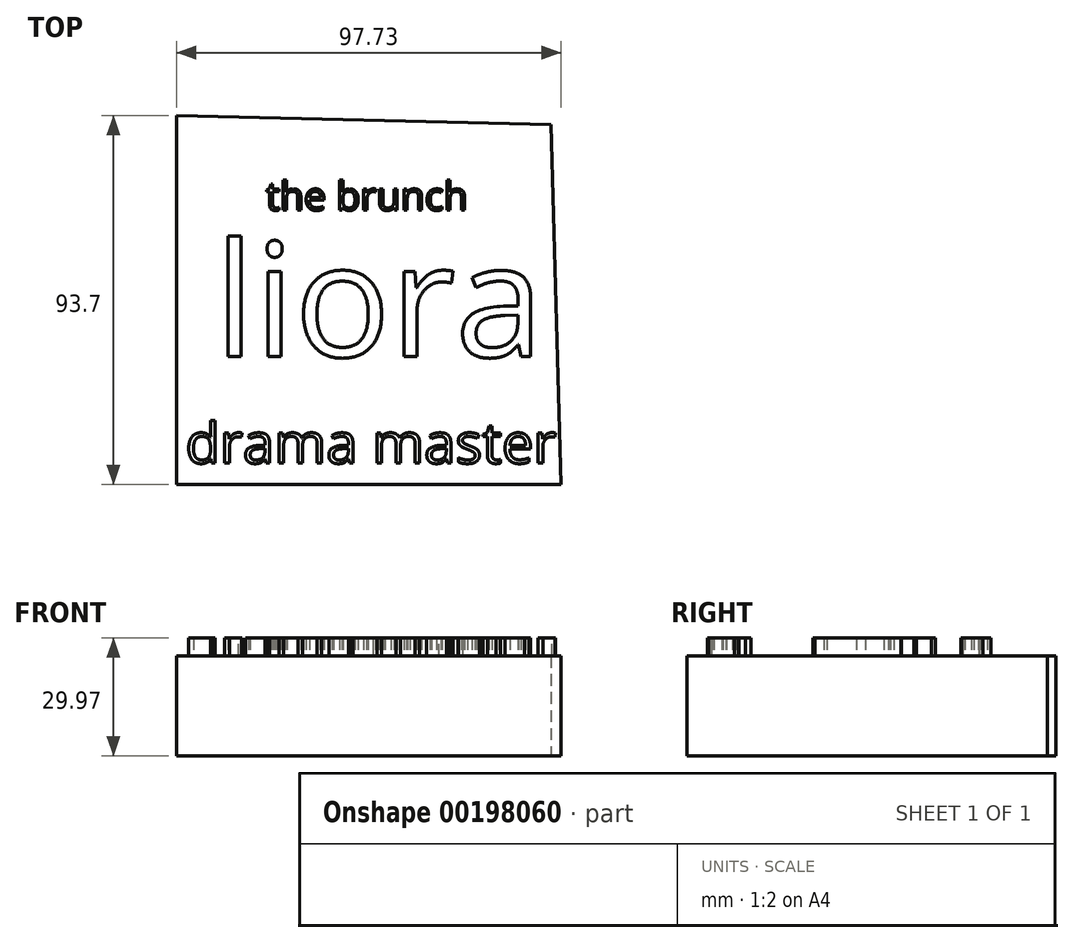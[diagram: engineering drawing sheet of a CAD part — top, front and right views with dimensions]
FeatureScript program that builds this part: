
annotation { "Feature Type Name" : "Feature", "Feature Type Description" : "" }
export const myFeature = defineFeature(function(context is Context, id is Id, definition is map)
    precondition{}
    {
        {
            var Q0;
            Q0=qCreatedBy(makeId("Top.planeOp"),FACE);
            var sketch = newSketch(context, id + "F0", { "sketchPlane" : qUnion([Q0])});
            skLineSegment(sketch, "E0", {"start": v(-49.97, 46) * mm, "end": v(-49.97, -47.7) * mm});
            skLineSegment(sketch, "E1", {"start": v(-49.97, -47.7) * mm, "end": v(47.76, -47.7) * mm});
            skLineSegment(sketch, "E2", {"start": v(47.76, -47.7) * mm, "end": v(45.16, 43.8) * mm});
            skLineSegment(sketch, "E3", {"start": v(45.16, 43.8) * mm, "end": v(-49.97, 46) * mm});
            skSolve(sketch);
        }
        {
            var Q0;
            Q0=makeQuery(id+"F0.imprint","IMPRINT",FACE,{"disambiguationData":[TD([[makeQuery(id+"F0.imprint","IMPRINT",EDGE,{"derivedFrom":sQuery(id+"F0.wireOp",EDGE,"E0")}),1.0]])]});
            extrude(context, id + "F1", {"entities" : qUnion([Q0]), "depth" : 25.4 * mm});
        }
        {
            var Q0;
            Q0=makeQuery(id+"F1.opExtrude","CAP_FACE",FACE,{"disambiguationData":[OSD([sQuery(id+"F0.wireOp",EDGE,"E0"),sQuery(id+"F0.wireOp",EDGE,"E1"),sQuery(id+"F0.wireOp",EDGE,"E2"),sQuery(id+"F0.wireOp",EDGE,"E3")])],"isStart":false});
            var sketch = newSketch(context, id + "F2", { "sketchPlane" : qUnion([Q0])});
            skText(sketch, "E4", { "text": "liora", "fontName": "OpenSans-Regular.ttf"});
            const initialGuessF2  = {"E4": [-0.04032, -0.01524, 1, 0, 0.02903]};
            skSetInitialGuess(sketch, initialGuessF2);
            skSolve(sketch);
        }
        {
            var Q0;
            Q0=makeQuery(id+"F2.imprint","IMPRINT",FACE,{"disambiguationData":[TD([[makeQuery(id+"F2.imprint","IMPRINT",EDGE,{"derivedFrom":sQuery(id+"F2.wireOp",EDGE,"E4.sketch_text.stroke-0")}),1.0]])]});
            var sketch = newSketch(context, id + "F3", { "sketchPlane" : qUnion([Q0])});
            skText(sketch, "E5", { "text": "drama master", "fontName": "OpenSans-Regular.ttf"});
            const initialGuessF3  = {"E5": [-0.04763, -0.0423, 1, 0, 0.01026]};
            skSetInitialGuess(sketch, initialGuessF3);
            skSolve(sketch);
        }
        {
            var Q0;
            Q0=makeQuery(id+"F2.imprint","IMPRINT",FACE,{"disambiguationData":[TD([[makeQuery(id+"F2.imprint","IMPRINT",EDGE,{"derivedFrom":sQuery(id+"F2.wireOp",EDGE,"E4.sketch_text.stroke-0")}),1.0]])]});
            var sketch = newSketch(context, id + "F4", { "sketchPlane" : qUnion([Q0])});
            skText(sketch, "E6", { "text": "the brunch", "fontName": "OpenSans-Regular.ttf"});
            const initialGuessF4  = {"E6": [-0.02722, 0.02198, 1, 0, 0.0072]};
            skSetInitialGuess(sketch, initialGuessF4);
            skSolve(sketch);
        }
        {
            var Q0;
            Q0 = qSketchRegion(id + "F4", true);
            var Q1;
            Q1=makeQuery(id+"F2.imprint","IMPRINT",FACE,{"disambiguationData":[TD([[makeQuery(id+"F2.imprint","IMPRINT",EDGE,{"derivedFrom":sQuery(id+"F2.wireOp",EDGE,"E4.sketch_text.stroke-4")}),-1.0]])]});
            var Q2;
            Q2=makeQuery(id+"F2.imprint","IMPRINT",FACE,{"disambiguationData":[TD([[makeQuery(id+"F2.imprint","IMPRINT",EDGE,{"derivedFrom":sQuery(id+"F2.wireOp",EDGE,"E4.sketch_text.stroke-8")}),-1.0]])]});
            var Q3;
            Q3=makeQuery(id+"F2.imprint","IMPRINT",FACE,{"disambiguationData":[TD([[makeQuery(id+"F2.imprint","IMPRINT",EDGE,{"derivedFrom":sQuery(id+"F2.wireOp",EDGE,"E4.sketch_text.stroke-0")}),-1.0]])]});
            var Q4;
            Q4=makeQuery(id+"F2.imprint","IMPRINT",FACE,{"disambiguationData":[TD([[makeQuery(id+"F2.imprint","IMPRINT",EDGE,{"derivedFrom":sQuery(id+"F2.wireOp",EDGE,"E4.sketch_text.stroke-16")}),-1.0]])]});
            var Q5;
            Q5=makeQuery(id+"F2.imprint","IMPRINT",FACE,{"disambiguationData":[TD([[makeQuery(id+"F2.imprint","IMPRINT",EDGE,{"derivedFrom":sQuery(id+"F2.wireOp",EDGE,"E4.sketch_text.stroke-33")}),-1.0]])]});
            var Q6;
            Q6=makeQuery(id+"F2.imprint","IMPRINT",FACE,{"disambiguationData":[TD([[makeQuery(id+"F2.imprint","IMPRINT",EDGE,{"derivedFrom":sQuery(id+"F2.wireOp",EDGE,"E4.sketch_text.stroke-46")}),-1.0]])]});
            var Q7;
            Q7 = qSketchRegion(id + "F3", true);
            extrude(context, id + "F5", {"entities" : qUnion([Q0, Q1, Q2, Q3, Q4, Q5, Q6, Q7]), "operationType" : NewBodyOperationType.ADD, "depth" : 4.57 * mm});
        }
    });
